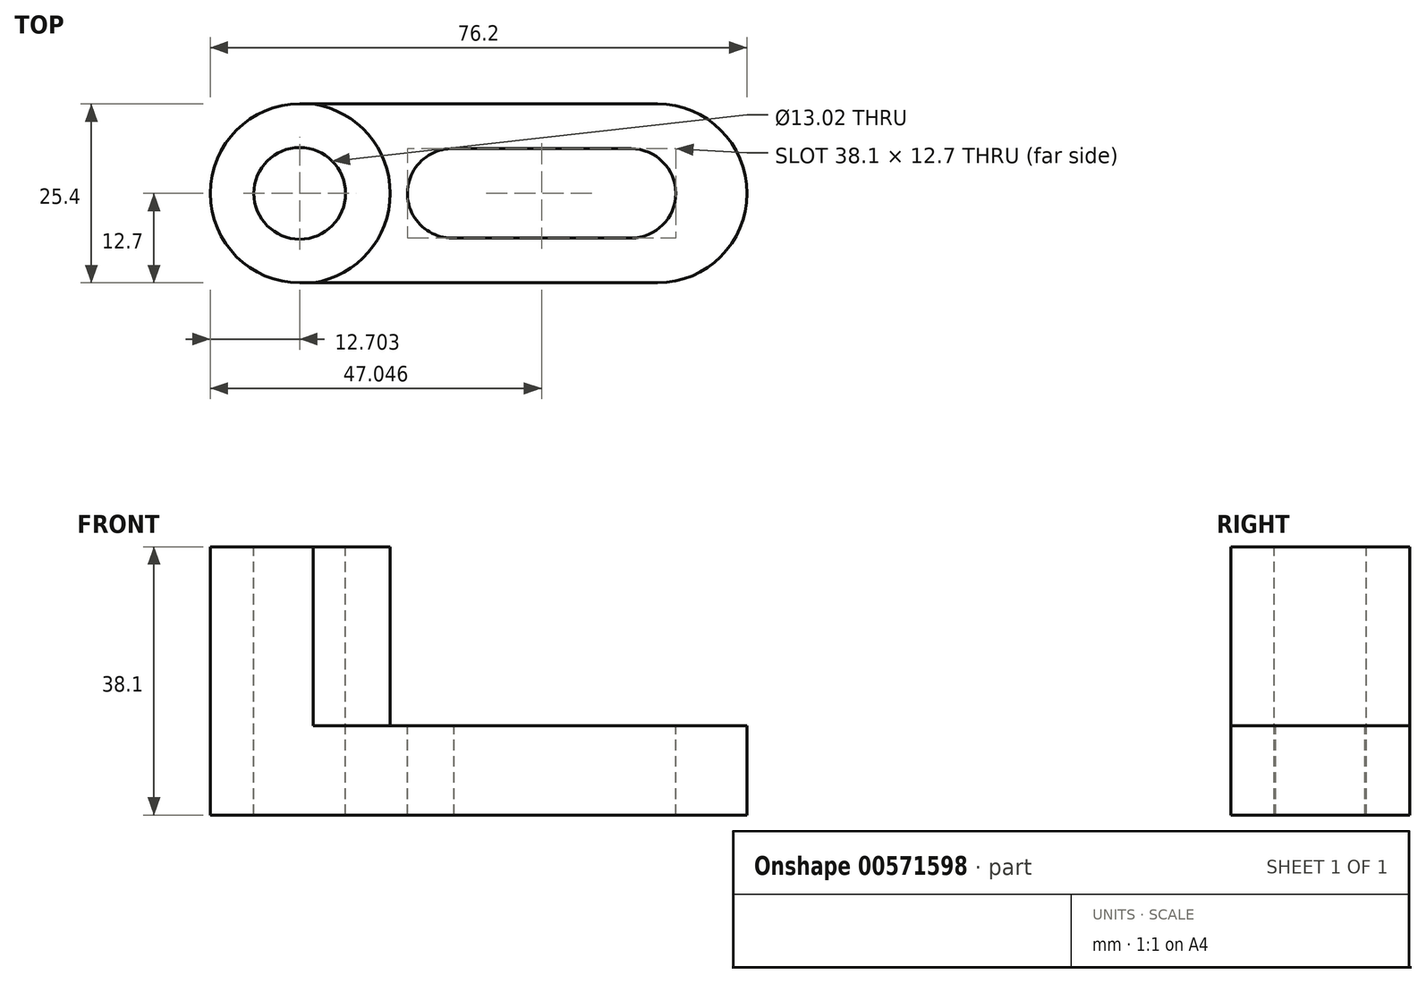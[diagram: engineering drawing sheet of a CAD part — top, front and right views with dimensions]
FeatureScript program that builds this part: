
annotation { "Feature Type Name" : "Feature", "Feature Type Description" : "" }
export const myFeature = defineFeature(function(context is Context, id is Id, definition is map)
    precondition{}
    {
        {
            var Q0;
            Q0=qCreatedBy(makeId("Top.planeOp"),FACE);
            var sketch = newSketch(context, id + "F0", { "sketchPlane" : qUnion([Q0])});
            skLineSegment(sketch, "E0", {"start": v(-24.18, 0) * mm, "end": v(26.62, 0) * mm});
            skLineSegment(sketch, "E1", {"start": v(26.62, 0) * mm, "end": v(26.62, -25.4) * mm});
            skLineSegment(sketch, "E2", {"start": v(26.62, -25.4) * mm, "end": v(-24.18, -25.4) * mm});
            skLineSegment(sketch, "E3", {"start": v(-24.18, -25.4) * mm, "end": v(-24.18, 0) * mm});
            skArc(sketch, "E4", {"start": v(26.62, -25.4) * mm, "mid": v(39.32, -12.7) * mm, "end": v(26.62, 0) * mm});
            skArc(sketch, "E5", {"start": v(-24.18, 0) * mm, "mid": v(-36.88, -12.7) * mm, "end": v(-24.18, -25.4) * mm});
            skSolve(sketch);
        }
        {
            var Q0;
            Q0=makeQuery(id+"F0.imprint","IMPRINT",FACE,{"disambiguationData":[TD([[makeQuery(id+"F0.imprint","IMPRINT",EDGE,{"derivedFrom":sQuery(id+"F0.wireOp",EDGE,"E0")}),-1.0]])]});
            var Q1;
            Q1=makeQuery(id+"F0.imprint","IMPRINT",FACE,{"disambiguationData":[TD([[makeQuery(id+"F0.imprint","IMPRINT",EDGE,{"derivedFrom":sQuery(id+"F0.wireOp",EDGE,"E3")}),1.0]])]});
            var Q2;
            Q2=makeQuery(id+"F0.imprint","IMPRINT",FACE,{"disambiguationData":[TD([[makeQuery(id+"F0.imprint","IMPRINT",EDGE,{"derivedFrom":sQuery(id+"F0.wireOp",EDGE,"E1")}),1.0]])]});
            extrude(context, id + "F1", {"entities" : qUnion([Q0, Q1, Q2]), "depth" : 12.7 * mm, "offsetDistance" : 25.4 * mm});
        }
        {
            var Q0;
            Q0=makeQuery(id+"F1.opExtrude","CAP_FACE",FACE,{"disambiguationData":[OSD([sQuery(id+"F0.wireOp",EDGE,"E0"),sQuery(id+"F0.wireOp",EDGE,"E2"),sQuery(id+"F0.wireOp",EDGE,"E4"),sQuery(id+"F0.wireOp",EDGE,"E5")])],"isStart":false});
            var sketch = newSketch(context, id + "F2", { "sketchPlane" : qUnion([Q0])});
            skCircle(sketch, "E6", {"center": v(-24.18, -12.7) * mm, "radius": 12.84 * mm});
            skSolve(sketch);
        }
        {
            var Q0;
            {var subQ5=makeQuery(id+"F1.opExtrude","CAP_EDGE",EDGE,{"disambiguationData":[OSD([sQuery(id+"F0.wireOp",EDGE,"E5")])],"isStart":false});Q0=makeQuery(id+"F2.imprint","IMPRINT",FACE,{"disambiguationData":[TD([[makeQuery(id+"F2.imprint","IMPRINT",EDGE,{"derivedFrom":subQ5}),1.0]])]});}
            extrude(context, id + "F3", {"entities" : qUnion([Q0]), "operationType" : NewBodyOperationType.ADD, "depth" : 25.4 * mm, "offsetDistance" : 25.4 * mm});
        }
        {
            var Q0;
            Q0=makeQuery(id+"F3.opExtrude","CAP_FACE",FACE,{"disambiguationData":[OSD([sQuery(id+"F0.wireOp",EDGE,"E0"),sQuery(id+"F0.wireOp",EDGE,"E2"),sQuery(id+"F0.wireOp",EDGE,"E5"),sQuery(id+"F2.wireOp",EDGE,"E6")])],"isStart":false});
            var sketch = newSketch(context, id + "F4", { "sketchPlane" : qUnion([Q0])});
            skCircle(sketch, "E7", {"center": v(-24.18, -12.7) * mm, "radius": 6.51 * mm});
            skSolve(sketch);
        }
        {
            var Q0;
            Q0=makeQuery(id+"F4.imprint","IMPRINT",FACE,{"disambiguationData":[TD([[makeQuery(id+"F4.imprint","IMPRINT",EDGE,{"derivedFrom":sQuery(id+"F4.wireOp",EDGE,"E7")}),1.0]])]});
            extrude(context, id + "F5", {"entities" : qUnion([Q0]), "operationType" : NewBodyOperationType.REMOVE, "oppositeDirection" : true, "depth" : 38.1 * mm, "offsetDistance" : 25.4 * mm});
        }
        {
            var Q0;
            Q0=makeQuery(id+"F1.opExtrude","CAP_FACE",FACE,{"disambiguationData":[OSD([sQuery(id+"F0.wireOp",EDGE,"E0"),sQuery(id+"F0.wireOp",EDGE,"E2"),sQuery(id+"F0.wireOp",EDGE,"E4"),sQuery(id+"F0.wireOp",EDGE,"E5")])],"isStart":false});
            var sketch = newSketch(context, id + "F6", { "sketchPlane" : qUnion([Q0])});
            skLineSegment(sketch, "E8", {"start": v(-2.27, -6.35) * mm, "end": v(22.87, -6.35) * mm});
            skLineSegment(sketch, "E9", {"start": v(22.87, -6.35) * mm, "end": v(22.87, -19.05) * mm});
            skLineSegment(sketch, "E10", {"start": v(22.87, -19.05) * mm, "end": v(-2.53, -19.05) * mm});
            skLineSegment(sketch, "E11", {"start": v(-2.53, -19.05) * mm, "end": v(-2.27, -6.35) * mm});
            skArc(sketch, "E12", {"start": v(-2.27, -6.35) * mm, "mid": v(-8.89, -12.56) * mm, "end": v(-2.53, -19.05) * mm});
            skArc(sketch, "E13", {"start": v(22.87, -19.05) * mm, "mid": v(29.22, -12.7) * mm, "end": v(22.87, -6.35) * mm});
            skSolve(sketch);
        }
        {
            var Q0;
            Q0=makeQuery(id+"F6.imprint","IMPRINT",FACE,{"disambiguationData":[TD([[makeQuery(id+"F6.imprint","IMPRINT",EDGE,{"derivedFrom":sQuery(id+"F6.wireOp",EDGE,"E9")}),1.0]])]});
            var Q1;
            Q1=makeQuery(id+"F6.imprint","IMPRINT",FACE,{"disambiguationData":[TD([[makeQuery(id+"F6.imprint","IMPRINT",EDGE,{"derivedFrom":sQuery(id+"F6.wireOp",EDGE,"E8")}),-1.0]])]});
            var Q2;
            Q2=makeQuery(id+"F6.imprint","IMPRINT",FACE,{"disambiguationData":[TD([[makeQuery(id+"F6.imprint","IMPRINT",EDGE,{"derivedFrom":sQuery(id+"F6.wireOp",EDGE,"E11")}),1.0]])]});
            extrude(context, id + "F7", {"entities" : qUnion([Q0, Q1, Q2]), "operationType" : NewBodyOperationType.REMOVE, "oppositeDirection" : true, "depth" : 12.7 * mm, "offsetDistance" : 25.4 * mm});
        }
    });
